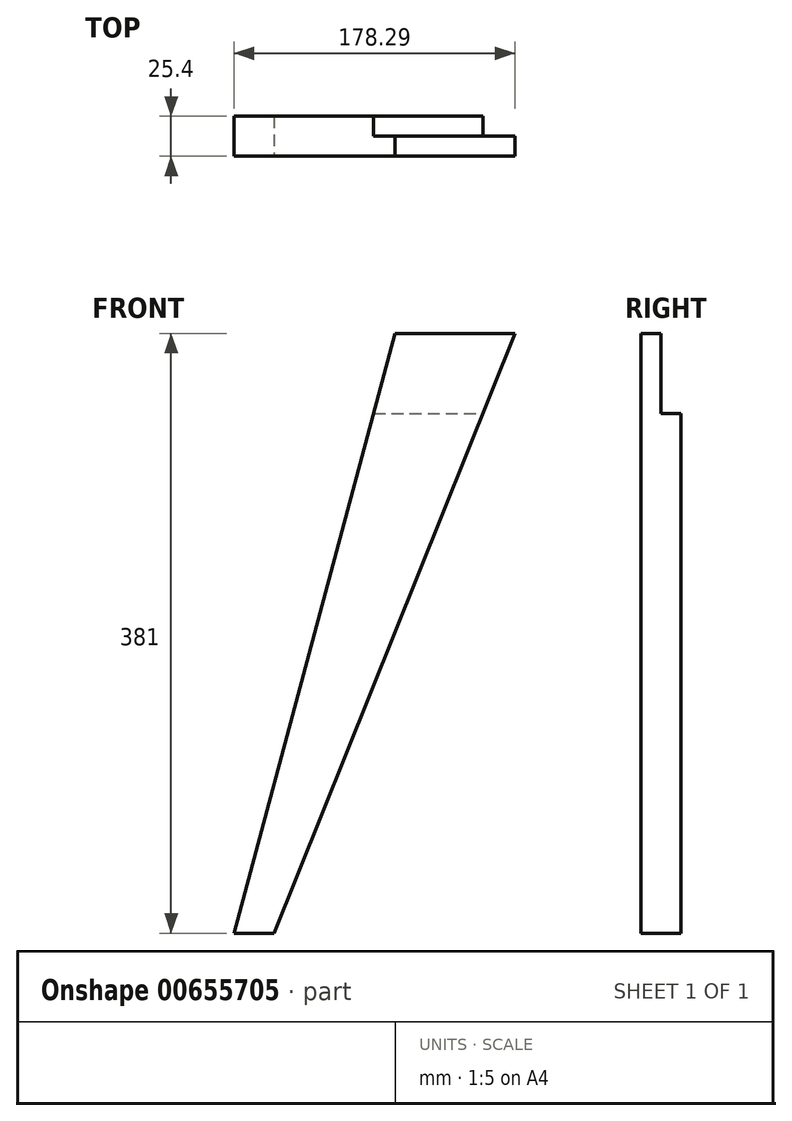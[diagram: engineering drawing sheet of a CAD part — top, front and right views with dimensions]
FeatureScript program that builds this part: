
annotation { "Feature Type Name" : "Feature", "Feature Type Description" : "" }
export const myFeature = defineFeature(function(context is Context, id is Id, definition is map)
    precondition{}
    {
        {
            var Q0;
            Q0=qCreatedBy(makeId("Front.planeOp"),FACE);
            var sketch = newSketch(context, id + "F0", { "sketchPlane" : qUnion([Q0])});
            skLineSegment(sketch, "E0", {"start": v(0, 0) * mm, "end": v(25.4, 0) * mm});
            skLineSegment(sketch, "E1", {"start": v(25.4, 0) * mm, "end": v(178.29, 381) * mm});
            skLineSegment(sketch, "E2", {"start": v(178.29, 381) * mm, "end": v(102.09, 381) * mm});
            skLineSegment(sketch, "E3", {"start": v(102.09, 381) * mm, "end": v(0, 0) * mm});
            skSolve(sketch);
        }
        {
            var Q0;
            Q0=makeQuery(id+"F0.imprint","IMPRINT",FACE,{"disambiguationData":[TD([[makeQuery(id+"F0.imprint","IMPRINT",EDGE,{"derivedFrom":sQuery(id+"F0.wireOp",EDGE,"E0")}),1.0]])]});
            extrude(context, id + "F1", {"entities" : qUnion([Q0]), "oppositeDirection" : true, "depth" : 25.4 * mm, "offsetDistance" : 25.4 * mm});
        }
        {
            var Q0;
            Q0=makeQuery(id+"F1.opExtrude","CAP_FACE",FACE,{"disambiguationData":[OSD([sQuery(id+"F0.wireOp",EDGE,"E0"),sQuery(id+"F0.wireOp",EDGE,"E1"),sQuery(id+"F0.wireOp",EDGE,"E2"),sQuery(id+"F0.wireOp",EDGE,"E3")])],"isStart":false});
            var sketch = newSketch(context, id + "F2", { "sketchPlane" : qUnion([Q0])});
            skLineSegment(sketch, "E4", {"start": v(-102.09, 381) * mm, "end": v(-88.48, 330.2) * mm});
            skLineSegment(sketch, "E5", {"start": v(-88.48, 330.2) * mm, "end": v(-157.9, 330.2) * mm});
            skLineSegment(sketch, "E6", {"start": v(-157.9, 330.2) * mm, "end": v(-178.29, 381) * mm});
            skLineSegment(sketch, "E7", {"start": v(-178.29, 381) * mm, "end": v(-102.09, 381) * mm});
            skSolve(sketch);
        }
        {
            var Q0;
            Q0=makeQuery(id+"F2.imprint","IMPRINT",FACE,{"disambiguationData":[TD([[makeQuery(id+"F2.imprint","IMPRINT",EDGE,{"derivedFrom":sQuery(id+"F2.wireOp",EDGE,"E4")}),-1.0]])]});
            extrude(context, id + "F3", {"entities" : qUnion([Q0]), "operationType" : NewBodyOperationType.REMOVE, "oppositeDirection" : true, "depth" : 12.7 * mm, "offsetDistance" : 25.4 * mm});
        }
    });
